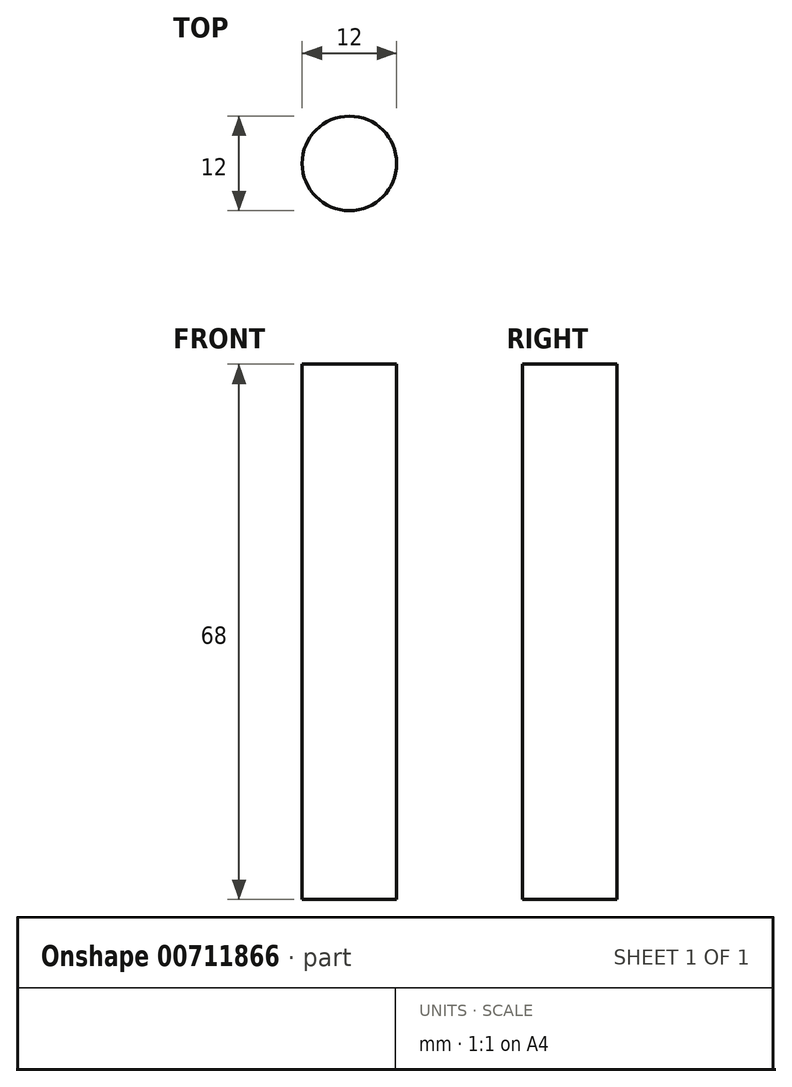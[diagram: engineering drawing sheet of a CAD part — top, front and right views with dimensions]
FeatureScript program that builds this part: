
annotation { "Feature Type Name" : "Feature", "Feature Type Description" : "" }
export const myFeature = defineFeature(function(context is Context, id is Id, definition is map)
    precondition{}
    {
        {
            var Q0;
            Q0=qCreatedBy(makeId("Top.planeOp"),FACE);
            var sketch = newSketch(context, id + "F0", { "sketchPlane" : qUnion([Q0])});
            skCircle(sketch, "E0", {"center": v(0, 0) * mm, "radius": 6 * mm});
            skSolve(sketch);
        }
        {
            var Q0;
            Q0 = qSketchRegion(id + "F0", true);
            extrude(context, id + "F1", {"entities" : qUnion([Q0]), "depth" : 68 * mm, "offsetDistance" : 25 * mm});
        }
    });
